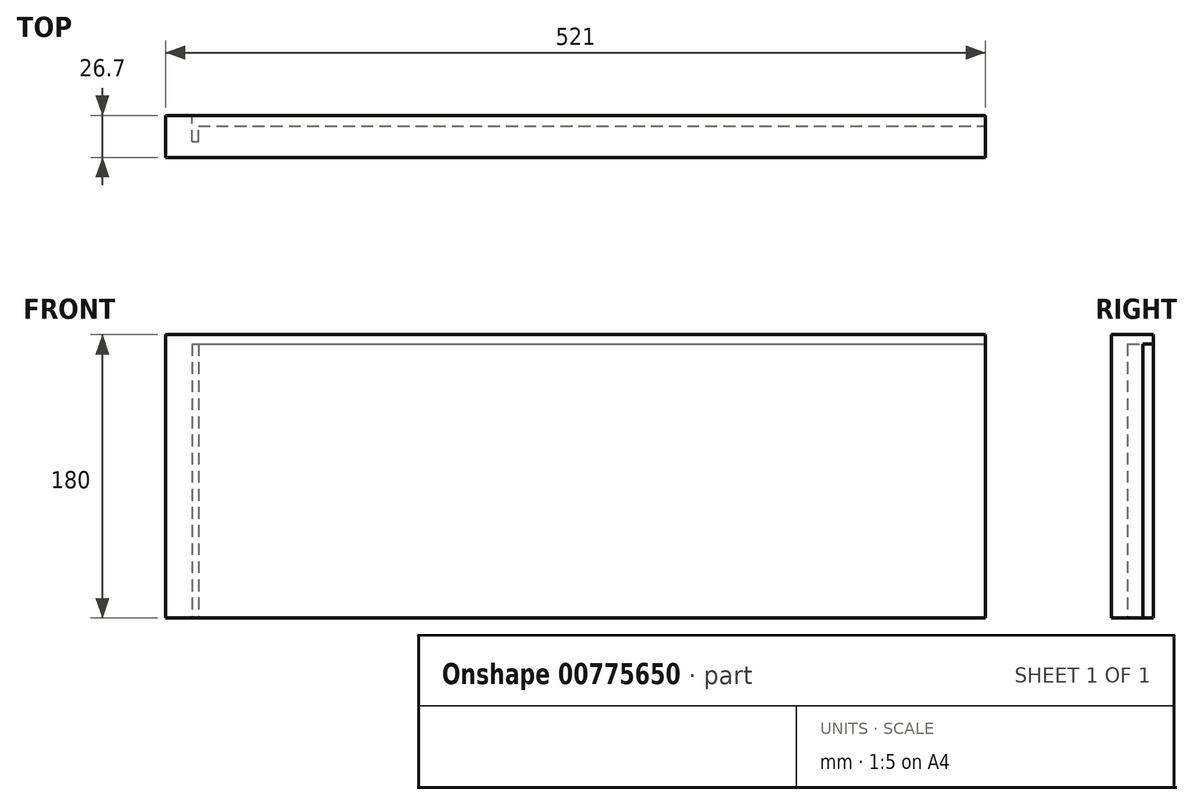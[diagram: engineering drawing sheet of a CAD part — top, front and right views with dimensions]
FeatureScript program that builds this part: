
annotation { "Feature Type Name" : "Feature", "Feature Type Description" : "" }
export const myFeature = defineFeature(function(context is Context, id is Id, definition is map)
    precondition{}
    {
        {
            var Q0;
            Q0=qCreatedBy(makeId("Top.planeOp"),FACE);
            var sketch = newSketch(context, id + "F0", { "sketchPlane" : qUnion([Q0])});
            skLineSegment(sketch, "E0", {"start": v(-128.48, 41.8) * mm, "end": v(392.52, 41.8) * mm});
            skLineSegment(sketch, "E1", {"start": v(-128.48, 41.8) * mm, "end": v(-128.48, 68.5) * mm});
            skLineSegment(sketch, "E2", {"start": v(-128.48, 68.5) * mm, "end": v(-111.48, 68.5) * mm});
            skLineSegment(sketch, "E3", {"start": v(-111.48, 68.5) * mm, "end": v(-111.48, 51.8) * mm});
            skLineSegment(sketch, "E4", {"start": v(-111.48, 51.8) * mm, "end": v(-107.48, 51.8) * mm});
            skLineSegment(sketch, "E5", {"start": v(-107.48, 51.8) * mm, "end": v(-107.48, 61.8) * mm});
            skLineSegment(sketch, "E6", {"start": v(-107.48, 61.8) * mm, "end": v(392.52, 61.8) * mm});
            skLineSegment(sketch, "E7", {"start": v(392.52, 41.8) * mm, "end": v(392.52, 61.8) * mm});
            skSolve(sketch);
        }
        {
            var Q0;
            Q0 = qSketchRegion(id + "F0", true);
            extrude(context, id + "F1", {"entities" : qUnion([Q0]), "depth" : 180 * mm, "offsetDistance" : 25 * mm});
        }
        {
            var Q0;
            Q0=makeQuery(id+"F1.opExtrude","SWEPT_FACE",FACE,{"disambiguationData":[OSD([sQuery(id+"F0.wireOp",EDGE,"E6")])]});
            var sketch = newSketch(context, id + "F2", { "sketchPlane" : qUnion([Q0])});
            skLineSegment(sketch, "E8", {"start": v(-392.52, 180) * mm, "end": v(114.48, 180) * mm});
            skLineSegment(sketch, "E9", {"start": v(114.48, 180) * mm, "end": v(114.48, 174) * mm});
            skLineSegment(sketch, "E10", {"start": v(114.48, 174) * mm, "end": v(-392.52, 174) * mm});
            skLineSegment(sketch, "E11", {"start": v(-392.52, 174) * mm, "end": v(-392.52, 180) * mm});
            skLineSegment(sketch, "E12", {"start": v(114.48, 174) * mm, "end": v(107.48, 174) * mm});
            skLineSegment(sketch, "E13", {"start": v(107.48, 174) * mm, "end": v(107.48, 180) * mm});
            skLineSegment(sketch, "E14", {"start": v(107.48, 180) * mm, "end": v(114.48, 180) * mm});
            skSolve(sketch);
        }
        {
            var Q0;
            Q0 = qSketchRegion(id + "F2", true);
            extrude(context, id + "F3", {"entities" : qUnion([Q0]), "operationType" : NewBodyOperationType.ADD, "depth" : 6.7 * mm, "offsetDistance" : 25 * mm});
        }
        {
            var Q0;
            Q0 = qSketchRegion(id + "F2", true);
            extrude(context, id + "F4", {"entities" : qUnion([Q0]), "operationType" : NewBodyOperationType.ADD, "oppositeDirection" : true, "depth" : 10 * mm, "offsetDistance" : 25 * mm});
        }
    });
